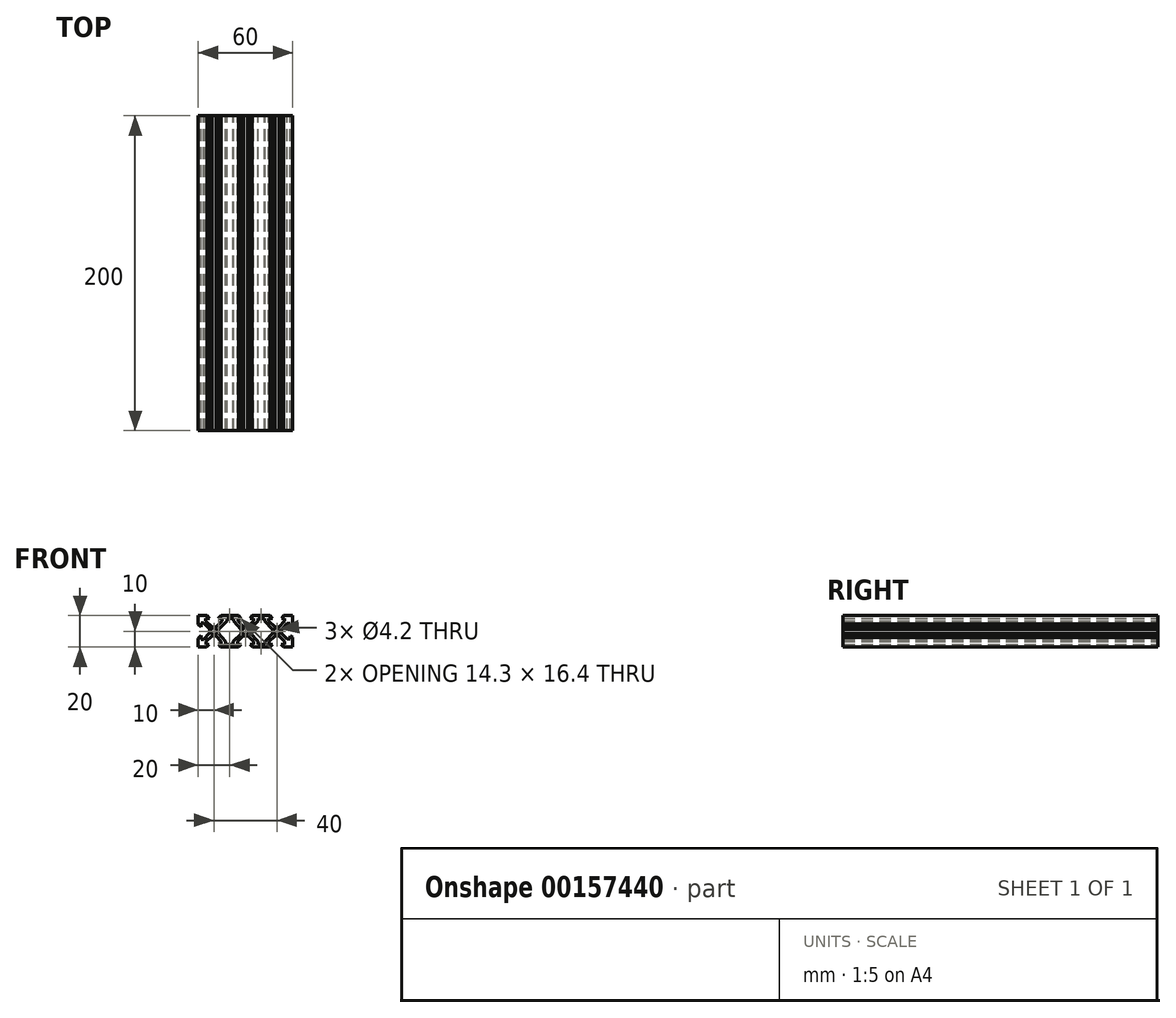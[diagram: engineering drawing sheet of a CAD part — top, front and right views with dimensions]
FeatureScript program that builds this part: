
annotation { "Feature Type Name" : "Feature", "Feature Type Description" : "" }
export const myFeature = defineFeature(function(context is Context, id is Id, definition is map)
    precondition{}
    {
        {
            var Q0;
            Q0=qCreatedBy(makeId("Front.planeOp"),FACE);
            var sketch = newSketch(context, id + "F0", { "sketchPlane" : qUnion([Q0])});
            skLineSegment(sketch, "E0.bottom", {"start": v(30, 10) * mm, "end": v(24.23, 10) * mm});
            skLineSegment(sketch, "E0.top", {"start": v(30, -10) * mm, "end": v(24.23, -10) * mm});
            skLineSegment(sketch, "E0.left", {"start": v(30, 10) * mm, "end": v(30, 4.56) * mm});
            skLineSegment(sketch, "E0.right", {"start": v(-30, 10) * mm, "end": v(-30, 4.4) * mm});
            skPoint(sketch, "E0.middle", {"position": v(0, 0) * mm});
            skLineSegment(sketch, "E1.0", {"start": v(-28.2, 8.2) * mm, "end": v(-28.2, 2.7) * mm});
            skLineSegment(sketch, "E1.1", {"start": v(28.2, 8.2) * mm, "end": v(22.92, 8.2) * mm});
            skLineSegment(sketch, "E1.2", {"start": v(28.2, 8.2) * mm, "end": v(28.2, 2.93) * mm});
            skLineSegment(sketch, "E1.3", {"start": v(28.2, -8.2) * mm, "end": v(22.78, -8.2) * mm});
            skCircle(sketch, "E2", {"center": v(0, 0) * mm, "radius": 2.1 * mm});
            skCircle(sketch, "E3", {"center": v(-20, 0) * mm, "radius": 2.1 * mm});
            skCircle(sketch, "E4", {"center": v(20, 0) * mm, "radius": 2.1 * mm});
            skLineSegment(sketch, "E5", {"start": v(-30, 4.4) * mm, "end": v(-28.2, 2.7) * mm});
            skLineSegment(sketch, "E6", {"start": v(-30, -4.47) * mm, "end": v(-28.2, -2.76) * mm});
            skLineSegment(sketch, "E7", {"start": v(-24.21, 10) * mm, "end": v(-22.7, 8.2) * mm});
            skLineSegment(sketch, "E8", {"start": v(-17.28, 8.2) * mm, "end": v(-15.53, 10) * mm});
            skLineSegment(sketch, "E9", {"start": v(-24.77, -10) * mm, "end": v(-23.06, -8.2) * mm});
            skLineSegment(sketch, "E10", {"start": v(-17.09, -8.2) * mm, "end": v(-15.66, -10) * mm});
            skLineSegment(sketch, "E11", {"start": v(2.9, 8.2) * mm, "end": v(4.22, 10) * mm});
            skLineSegment(sketch, "E12", {"start": v(-4.42, -10) * mm, "end": v(-2.88, -8.2) * mm});
            skLineSegment(sketch, "E13", {"start": v(2.82, -8.2) * mm, "end": v(4.44, -10) * mm});
            skLineSegment(sketch, "E14", {"start": v(15.72, 10) * mm, "end": v(17.27, 8.2) * mm});
            skLineSegment(sketch, "E15", {"start": v(22.92, 8.2) * mm, "end": v(24.23, 10) * mm});
            skLineSegment(sketch, "E16", {"start": v(15.6, -10) * mm, "end": v(17.12, -8.2) * mm});
            skLineSegment(sketch, "E17", {"start": v(22.78, -8.2) * mm, "end": v(24.23, -10) * mm});
            skLineSegment(sketch, "E18", {"start": v(28.2, -2.83) * mm, "end": v(30, -4) * mm});
            skLineSegment(sketch, "E19", {"start": v(28.2, 2.93) * mm, "end": v(30, 4.56) * mm});
            skLineSegment(sketch, "E20.bottom", {"start": v(-17.15, 2.85) * mm, "end": v(-22.85, 2.85) * mm});
            skLineSegment(sketch, "E20.top", {"start": v(-17.15, -2.85) * mm, "end": v(-22.85, -2.85) * mm});
            skLineSegment(sketch, "E20.left", {"start": v(-17.15, 2.85) * mm, "end": v(-17.15, -2.85) * mm});
            skLineSegment(sketch, "E20.right", {"start": v(-22.85, 2.85) * mm, "end": v(-22.85, -2.85) * mm});
            skLineSegment(sketch, "E21.bottom", {"start": v(2.85, 2.85) * mm, "end": v(-2.85, 2.85) * mm});
            skLineSegment(sketch, "E21.top", {"start": v(2.85, -2.85) * mm, "end": v(-2.85, -2.85) * mm});
            skLineSegment(sketch, "E21.left", {"start": v(2.85, 2.85) * mm, "end": v(2.85, -2.85) * mm});
            skLineSegment(sketch, "E21.right", {"start": v(-2.85, 2.85) * mm, "end": v(-2.85, -2.85) * mm});
            skLineSegment(sketch, "E22.bottom", {"start": v(22.85, 2.85) * mm, "end": v(17.15, 2.85) * mm});
            skLineSegment(sketch, "E22.top", {"start": v(22.85, -2.85) * mm, "end": v(17.15, -2.85) * mm});
            skLineSegment(sketch, "E22.left", {"start": v(22.85, 2.85) * mm, "end": v(22.85, -2.85) * mm});
            skLineSegment(sketch, "E22.right", {"start": v(17.15, 2.85) * mm, "end": v(17.15, -2.85) * mm});
            skLineSegment(sketch, "E23", {"start": v(-20, 2.1) * mm, "end": v(-44.26, 2.1) * mm, "construction": true});
            skPoint(sketch, "E23.startSnap0", {"position": v(-20, 2.85) * mm});
            skLineSegment(sketch, "E24", {"start": v(-19.99, -2.1) * mm, "end": v(-43.86, -2.1) * mm, "construction": true});
            skLineSegment(sketch, "E25.0", {"start": v(-26.56, 6.56) * mm, "end": v(-26.56, 5.27) * mm});
            skLineSegment(sketch, "E25.1", {"start": v(26.56, 6.56) * mm, "end": v(24.93, 6.56) * mm});
            skLineSegment(sketch, "E25.2", {"start": v(26.56, 6.56) * mm, "end": v(26.56, 4.88) * mm});
            skLineSegment(sketch, "E25.3", {"start": v(26.56, -6.56) * mm, "end": v(24.9, -6.56) * mm});
            skLineSegment(sketch, "E26", {"start": v(-25.2, 6.56) * mm, "end": v(-25.2, 8.2) * mm});
            skLineSegment(sketch, "E27", {"start": v(-26.56, 5.27) * mm, "end": v(-28.2, 5.27) * mm});
            skLineSegment(sketch, "E28", {"start": v(-25.2, 6.56) * mm, "end": v(-21.3, 2.85) * mm});
            skLineSegment(sketch, "E29", {"start": v(-26.56, 5.27) * mm, "end": v(-22.85, 1.46) * mm});
            skLineSegment(sketch, "E30", {"start": v(-26.56, -5.15) * mm, "end": v(-22.85, -1.11) * mm});
            skLineSegment(sketch, "E31", {"start": v(-24.9, -6.56) * mm, "end": v(-21.17, -2.85) * mm});
            skLineSegment(sketch, "E32", {"start": v(-26.56, -5.15) * mm, "end": v(-28.2, -5.15) * mm});
            skLineSegment(sketch, "E33", {"start": v(-24.9, -6.56) * mm, "end": v(-24.9, -8.2) * mm});
            skLineSegment(sketch, "E34", {"start": v(-14.86, 8.2) * mm, "end": v(-14.86, 6.56) * mm});
            skLineSegment(sketch, "E35", {"start": v(-14.86, 6.56) * mm, "end": v(-18.6, 2.85) * mm});
            skLineSegment(sketch, "E36", {"start": v(-17.15, 1.27) * mm, "end": v(-11.83, 6.56) * mm});
            skLineSegment(sketch, "E37", {"start": v(-2.77, 8.2) * mm, "end": v(-4.42, 10) * mm});
            skLineSegment(sketch, "E38", {"start": v(-18.74, -2.85) * mm, "end": v(-15.4, -6.56) * mm});
            skLineSegment(sketch, "E39", {"start": v(-15.4, -6.56) * mm, "end": v(-15.4, -8.2) * mm});
            skLineSegment(sketch, "E40", {"start": v(-17.15, -1.23) * mm, "end": v(-12.58, -6.56) * mm});
            skLineSegment(sketch, "E41", {"start": v(-1.3, 2.85) * mm, "end": v(-4.84, 6.56) * mm});
            skLineSegment(sketch, "E42", {"start": v(-4.84, 6.56) * mm, "end": v(-4.84, 8.2) * mm});
            skLineSegment(sketch, "E43", {"start": v(-2.85, 1.13) * mm, "end": v(-7.54, 6.56) * mm});
            skLineSegment(sketch, "E44", {"start": v(-2.85, -1.54) * mm, "end": v(-7.8, -6.56) * mm});
            skLineSegment(sketch, "E45", {"start": v(-1.46, -2.85) * mm, "end": v(-5.09, -6.56) * mm});
            skLineSegment(sketch, "E46", {"start": v(-5.09, -6.56) * mm, "end": v(-5.09, -8.2) * mm});
            skLineSegment(sketch, "E47", {"start": v(-12.58, -6.56) * mm, "end": v(-12.58, -8.2) * mm});
            skLineSegment(sketch, "E48", {"start": v(-7.8, -6.56) * mm, "end": v(-7.8, -8.2) * mm});
            skLineSegment(sketch, "E49", {"start": v(-7.54, 6.56) * mm, "end": v(-7.54, 8.2) * mm});
            skLineSegment(sketch, "E50", {"start": v(-11.83, 6.56) * mm, "end": v(-11.83, 8.2) * mm});
            skLineSegment(sketch, "E51", {"start": v(1.34, 2.85) * mm, "end": v(5.05, 6.56) * mm});
            skLineSegment(sketch, "E52", {"start": v(2.85, 1.12) * mm, "end": v(8, 6.56) * mm});
            skLineSegment(sketch, "E53", {"start": v(8, 6.56) * mm, "end": v(8, 8.2) * mm});
            skLineSegment(sketch, "E54", {"start": v(1.52, -2.85) * mm, "end": v(5.25, -6.56) * mm});
            skLineSegment(sketch, "E55", {"start": v(5.25, -6.5) * mm, "end": v(5.25, -8.2) * mm});
            skLineSegment(sketch, "E56", {"start": v(2.85, -1.1) * mm, "end": v(8, -6.56) * mm});
            skLineSegment(sketch, "E57", {"start": v(18.75, 2.85) * mm, "end": v(14.61, 6.56) * mm});
            skLineSegment(sketch, "E58", {"start": v(17.15, 1.18) * mm, "end": v(12.15, 6.56) * mm});
            skLineSegment(sketch, "E59", {"start": v(12.15, 6.51) * mm, "end": v(12.15, 8.2) * mm});
            skLineSegment(sketch, "E60", {"start": v(14.61, 6.56) * mm, "end": v(14.61, 8.2) * mm});
            skLineSegment(sketch, "E61", {"start": v(17.15, -1.45) * mm, "end": v(12.58, -6.56) * mm});
            skLineSegment(sketch, "E62", {"start": v(18.78, -2.85) * mm, "end": v(15.13, -6.56) * mm});
            skLineSegment(sketch, "E63", {"start": v(12.58, -6.56) * mm, "end": v(12.58, -8.2) * mm});
            skLineSegment(sketch, "E64", {"start": v(21.38, 2.85) * mm, "end": v(24.93, 6.56) * mm});
            skLineSegment(sketch, "E65", {"start": v(22.85, 1.03) * mm, "end": v(26.56, 4.88) * mm});
            skLineSegment(sketch, "E66", {"start": v(22.85, -1.37) * mm, "end": v(26.56, -4.98) * mm});
            skLineSegment(sketch, "E67", {"start": v(26.5, -4.98) * mm, "end": v(28.2, -4.98) * mm});
            skLineSegment(sketch, "E68", {"start": v(21.27, -2.85) * mm, "end": v(24.9, -6.56) * mm});
            skLineSegment(sketch, "E69", {"start": v(24.9, -6.5) * mm, "end": v(24.9, -8.2) * mm});
            skLineSegment(sketch, "E70.trimOffspring", {"start": v(-24.21, 10) * mm, "end": v(-30, 10) * mm});
            skLineSegment(sketch, "E71.trimOffspring", {"start": v(-22.7, 8.2) * mm, "end": v(-28.2, 8.2) * mm});
            skLineSegment(sketch, "E72.trimOffspring", {"start": v(-25.2, 6.56) * mm, "end": v(-26.56, 6.56) * mm});
            skLineSegment(sketch, "E73.trimOffspring", {"start": v(-28.2, -2.76) * mm, "end": v(-28.2, -8.2) * mm});
            skLineSegment(sketch, "E74.trimOffspring", {"start": v(-30, -4.47) * mm, "end": v(-30, -10) * mm});
            skLineSegment(sketch, "E75.trimOffspring", {"start": v(-26.56, -5.15) * mm, "end": v(-26.56, -6.56) * mm});
            skLineSegment(sketch, "E76.trimOffspring", {"start": v(-11.83, 6.56) * mm, "end": v(-14.86, 6.56) * mm});
            skLineSegment(sketch, "E77.trimOffspring", {"start": v(-12.58, -6.56) * mm, "end": v(-15.4, -6.56) * mm});
            skLineSegment(sketch, "E78.trimOffspring", {"start": v(-24.9, -6.56) * mm, "end": v(-26.56, -6.56) * mm});
            skLineSegment(sketch, "E79.trimOffspring", {"start": v(-23.06, -8.2) * mm, "end": v(-28.2, -8.2) * mm});
            skLineSegment(sketch, "E80.trimOffspring", {"start": v(-24.77, -10) * mm, "end": v(-30, -10) * mm});
            skLineSegment(sketch, "E81.trimOffspring", {"start": v(-4.42, 10) * mm, "end": v(-15.53, 10) * mm});
            skLineSegment(sketch, "E82", {"start": v(5.05, 6.56) * mm, "end": v(5.05, 8.2) * mm});
            skLineSegment(sketch, "E83.trimOffspring", {"start": v(-2.77, 8.2) * mm, "end": v(-17.28, 8.2) * mm});
            skLineSegment(sketch, "E84.trimOffspring", {"start": v(-4.84, 6.56) * mm, "end": v(-7.54, 6.56) * mm});
            skLineSegment(sketch, "E85.trimOffspring", {"start": v(8, 6.56) * mm, "end": v(5.05, 6.56) * mm});
            skLineSegment(sketch, "E86.trimOffspring", {"start": v(8, -6.56) * mm, "end": v(5.25, -6.56) * mm});
            skLineSegment(sketch, "E87.trimOffspring", {"start": v(-4.42, -10) * mm, "end": v(-15.66, -10) * mm});
            skLineSegment(sketch, "E88.trimOffspring", {"start": v(-2.88, -8.2) * mm, "end": v(-17.09, -8.2) * mm});
            skLineSegment(sketch, "E89.trimOffspring", {"start": v(-5.09, -6.56) * mm, "end": v(-7.8, -6.56) * mm});
            skLineSegment(sketch, "E90.trimOffspring", {"start": v(15.6, -10) * mm, "end": v(4.44, -10) * mm});
            skLineSegment(sketch, "E91", {"start": v(15.13, -6.56) * mm, "end": v(15.13, -8.2) * mm});
            skLineSegment(sketch, "E92.trimOffspring", {"start": v(17.12, -8.2) * mm, "end": v(2.82, -8.2) * mm});
            skLineSegment(sketch, "E93.trimOffspring", {"start": v(15.13, -6.56) * mm, "end": v(12.58, -6.56) * mm});
            skLineSegment(sketch, "E94.trimOffspring", {"start": v(30, -4) * mm, "end": v(30, -10) * mm});
            skLineSegment(sketch, "E95.trimOffspring", {"start": v(28.2, -2.83) * mm, "end": v(28.2, -8.2) * mm});
            skLineSegment(sketch, "E96.trimOffspring", {"start": v(26.56, -4.98) * mm, "end": v(26.56, -6.56) * mm});
            skLineSegment(sketch, "E97", {"start": v(24.93, 6.56) * mm, "end": v(24.93, 8.2) * mm});
            skLineSegment(sketch, "E98", {"start": v(26.56, 4.88) * mm, "end": v(28.2, 4.88) * mm});
            skLineSegment(sketch, "E99.trimOffspring", {"start": v(15.72, 10) * mm, "end": v(4.22, 10) * mm});
            skLineSegment(sketch, "E100.trimOffspring", {"start": v(17.27, 8.2) * mm, "end": v(2.9, 8.2) * mm});
            skLineSegment(sketch, "E101.trimOffspring", {"start": v(14.61, 6.56) * mm, "end": v(12.15, 6.56) * mm});
            skLineSegment(sketch, "E102", {"start": v(8, -6.56) * mm, "end": v(8, -8.2) * mm});
            skSolve(sketch);
        }
        {
            var Q0;
            Q0=makeQuery(id+"F0.imprint","IMPRINT",FACE,{"disambiguationData":[TD([[makeQuery(id+"F0.imprint","IMPRINT",EDGE,{"derivedFrom":sQuery(id+"F0.wireOp",EDGE,"E0.bottom")}),1.0]])]});
            var Q1;
            Q1=makeQuery(id+"F0.imprint","IMPRINT",FACE,{"disambiguationData":[TD([[makeQuery(id+"F0.imprint","IMPRINT",EDGE,{"derivedFrom":sQuery(id+"F0.wireOp",EDGE,"E25.1")}),-1.0]])]});
            var Q2;
            Q2=makeQuery(id+"F0.imprint","IMPRINT",FACE,{"disambiguationData":[TD([[makeQuery(id+"F0.imprint","IMPRINT",EDGE,{"derivedFrom":sQuery(id+"F0.wireOp",EDGE,"E25.1")}),1.0]])]});
            var Q3;
            {var subQ1=sQuery(id+"F0.wireOp",EDGE,"E25.3");Q3=makeQuery(id+"F0.imprint","IMPRINT",FACE,{"disambiguationData":[TD([[makeQuery(id+"F0.imprint","IMPRINT",EDGE,{"derivedFrom":subQ1}),1.0]])]});}
            var Q4;
            Q4=makeQuery(id+"F0.imprint","IMPRINT",FACE,{"disambiguationData":[TD([[makeQuery(id+"F0.imprint","IMPRINT",EDGE,{"derivedFrom":sQuery(id+"F0.wireOp",EDGE,"E0.top")}),-1.0]])]});
            var Q5;
            Q5=makeQuery(id+"F0.imprint","IMPRINT",FACE,{"disambiguationData":[TD([[makeQuery(id+"F0.imprint","IMPRINT",EDGE,{"derivedFrom":sQuery(id+"F0.wireOp",EDGE,"E25.3")}),-1.0]])]});
            var Q6;
            Q6=makeQuery(id+"F0.imprint","IMPRINT",FACE,{"disambiguationData":[TD([[makeQuery(id+"F0.imprint","IMPRINT",EDGE,{"derivedFrom":sQuery(id+"F0.wireOp",EDGE,"E4")}),-1.0]])]});
            var Q7;
            {var subQ1=sQuery(id+"F0.wireOp",EDGE,"E57");Q7=makeQuery(id+"F0.imprint","IMPRINT",FACE,{"disambiguationData":[TD([[makeQuery(id+"F0.imprint","IMPRINT",EDGE,{"derivedFrom":subQ1}),1.0]])]});}
            var Q8;
            {var subQ4=sQuery(id+"F0.wireOp",EDGE,"E60");Q8=makeQuery(id+"F0.imprint","IMPRINT",FACE,{"disambiguationData":[TD([[makeQuery(id+"F0.imprint","IMPRINT",EDGE,{"derivedFrom":subQ4}),1.0]])]});}
            var Q9;
            {var subQ3=sQuery(id+"F0.wireOp",EDGE,"E11");Q9=makeQuery(id+"F0.imprint","IMPRINT",FACE,{"disambiguationData":[TD([[makeQuery(id+"F0.imprint","IMPRINT",EDGE,{"derivedFrom":subQ3}),-1.0]])]});}
            var Q10;
            {var subQ0=sQuery(id+"F0.wireOp",EDGE,"E53");Q10=makeQuery(id+"F0.imprint","IMPRINT",FACE,{"disambiguationData":[TD([[makeQuery(id+"F0.imprint","IMPRINT",EDGE,{"derivedFrom":subQ0}),1.0]])]});}
            var Q11;
            {var subQ1=sQuery(id+"F0.wireOp",EDGE,"E51");Q11=makeQuery(id+"F0.imprint","IMPRINT",FACE,{"disambiguationData":[TD([[makeQuery(id+"F0.imprint","IMPRINT",EDGE,{"derivedFrom":subQ1}),-1.0]])]});}
            var Q12;
            {var subQ4=sQuery(id+"F0.wireOp",EDGE,"E61");Q12=makeQuery(id+"F0.imprint","IMPRINT",FACE,{"disambiguationData":[TD([[makeQuery(id+"F0.imprint","IMPRINT",EDGE,{"derivedFrom":subQ4}),1.0]])]});}
            var Q13;
            {var subQ0=sQuery(id+"F0.wireOp",EDGE,"E63");Q13=makeQuery(id+"F0.imprint","IMPRINT",FACE,{"disambiguationData":[TD([[makeQuery(id+"F0.imprint","IMPRINT",EDGE,{"derivedFrom":subQ0}),1.0]])]});}
            var Q14;
            {var subQ3=sQuery(id+"F0.wireOp",EDGE,"E13");Q14=makeQuery(id+"F0.imprint","IMPRINT",FACE,{"disambiguationData":[TD([[makeQuery(id+"F0.imprint","IMPRINT",EDGE,{"derivedFrom":subQ3}),1.0]])]});}
            var Q15;
            {var subQ0=sQuery(id+"F0.wireOp",EDGE,"E86.trimOffspring");Q15=makeQuery(id+"F0.imprint","IMPRINT",FACE,{"disambiguationData":[TD([[makeQuery(id+"F0.imprint","IMPRINT",EDGE,{"derivedFrom":subQ0}),1.0]])]});}
            var Q16;
            {var subQ1=sQuery(id+"F0.wireOp",EDGE,"E54");Q16=makeQuery(id+"F0.imprint","IMPRINT",FACE,{"disambiguationData":[TD([[makeQuery(id+"F0.imprint","IMPRINT",EDGE,{"derivedFrom":subQ1}),1.0]])]});}
            var Q17;
            Q17=makeQuery(id+"F0.imprint","IMPRINT",FACE,{"disambiguationData":[TD([[makeQuery(id+"F0.imprint","IMPRINT",EDGE,{"derivedFrom":sQuery(id+"F0.wireOp",EDGE,"E2")}),-1.0]])]});
            var Q18;
            {var subQ0=sQuery(id+"F0.wireOp",EDGE,"E41");Q18=makeQuery(id+"F0.imprint","IMPRINT",FACE,{"disambiguationData":[TD([[makeQuery(id+"F0.imprint","IMPRINT",EDGE,{"derivedFrom":subQ0}),1.0]])]});}
            var Q19;
            {var subQ0=sQuery(id+"F0.wireOp",EDGE,"E42");Q19=makeQuery(id+"F0.imprint","IMPRINT",FACE,{"disambiguationData":[TD([[makeQuery(id+"F0.imprint","IMPRINT",EDGE,{"derivedFrom":subQ0}),1.0]])]});}
            var Q20;
            {var subQ5=sQuery(id+"F0.wireOp",EDGE,"E8");Q20=makeQuery(id+"F0.imprint","IMPRINT",FACE,{"disambiguationData":[TD([[makeQuery(id+"F0.imprint","IMPRINT",EDGE,{"derivedFrom":subQ5}),-1.0]])]});}
            var Q21;
            {var subQ0=sQuery(id+"F0.wireOp",EDGE,"E34");Q21=makeQuery(id+"F0.imprint","IMPRINT",FACE,{"disambiguationData":[TD([[makeQuery(id+"F0.imprint","IMPRINT",EDGE,{"derivedFrom":subQ0}),1.0]])]});}
            var Q22;
            {var subQ0=sQuery(id+"F0.wireOp",EDGE,"E35");Q22=makeQuery(id+"F0.imprint","IMPRINT",FACE,{"disambiguationData":[TD([[makeQuery(id+"F0.imprint","IMPRINT",EDGE,{"derivedFrom":subQ0}),1.0]])]});}
            var Q23;
            {var subQ1=sQuery(id+"F0.wireOp",EDGE,"E44");Q23=makeQuery(id+"F0.imprint","IMPRINT",FACE,{"disambiguationData":[TD([[makeQuery(id+"F0.imprint","IMPRINT",EDGE,{"derivedFrom":subQ1}),1.0]])]});}
            var Q24;
            {var subQ0=sQuery(id+"F0.wireOp",EDGE,"E46");Q24=makeQuery(id+"F0.imprint","IMPRINT",FACE,{"disambiguationData":[TD([[makeQuery(id+"F0.imprint","IMPRINT",EDGE,{"derivedFrom":subQ0}),-1.0]])]});}
            var Q25;
            {var subQ3=sQuery(id+"F0.wireOp",EDGE,"E10");Q25=makeQuery(id+"F0.imprint","IMPRINT",FACE,{"disambiguationData":[TD([[makeQuery(id+"F0.imprint","IMPRINT",EDGE,{"derivedFrom":subQ3}),1.0]])]});}
            var Q26;
            {var subQ0=sQuery(id+"F0.wireOp",EDGE,"E39");Q26=makeQuery(id+"F0.imprint","IMPRINT",FACE,{"disambiguationData":[TD([[makeQuery(id+"F0.imprint","IMPRINT",EDGE,{"derivedFrom":subQ0}),1.0]])]});}
            var Q27;
            {var subQ0=sQuery(id+"F0.wireOp",EDGE,"E38");Q27=makeQuery(id+"F0.imprint","IMPRINT",FACE,{"disambiguationData":[TD([[makeQuery(id+"F0.imprint","IMPRINT",EDGE,{"derivedFrom":subQ0}),1.0]])]});}
            var Q28;
            Q28=makeQuery(id+"F0.imprint","IMPRINT",FACE,{"disambiguationData":[TD([[makeQuery(id+"F0.imprint","IMPRINT",EDGE,{"derivedFrom":sQuery(id+"F0.wireOp",EDGE,"E3")}),-1.0]])]});
            var Q29;
            Q29=makeQuery(id+"F0.imprint","IMPRINT",FACE,{"disambiguationData":[TD([[makeQuery(id+"F0.imprint","IMPRINT",EDGE,{"derivedFrom":sQuery(id+"F0.wireOp",EDGE,"E25.0")}),1.0]])]});
            var Q30;
            {var subQ1=sQuery(id+"F0.wireOp",EDGE,"E30");Q30=makeQuery(id+"F0.imprint","IMPRINT",FACE,{"disambiguationData":[TD([[makeQuery(id+"F0.imprint","IMPRINT",EDGE,{"derivedFrom":subQ1}),-1.0]])]});}
            var Q31;
            Q31=makeQuery(id+"F0.imprint","IMPRINT",FACE,{"disambiguationData":[TD([[makeQuery(id+"F0.imprint","IMPRINT",EDGE,{"derivedFrom":sQuery(id+"F0.wireOp",EDGE,"E25.0")}),-1.0]])]});
            var Q32;
            Q32=makeQuery(id+"F0.imprint","IMPRINT",FACE,{"disambiguationData":[TD([[makeQuery(id+"F0.imprint","IMPRINT",EDGE,{"derivedFrom":sQuery(id+"F0.wireOp",EDGE,"E0.right")}),1.0]])]});
            var Q33;
            {var subQ1=sQuery(id+"F0.wireOp",EDGE,"E32");Q33=makeQuery(id+"F0.imprint","IMPRINT",FACE,{"disambiguationData":[TD([[makeQuery(id+"F0.imprint","IMPRINT",EDGE,{"derivedFrom":subQ1}),1.0]])]});}
            var Q34;
            {var subQ4=sQuery(id+"F0.wireOp",EDGE,"E6");Q34=makeQuery(id+"F0.imprint","IMPRINT",FACE,{"disambiguationData":[TD([[makeQuery(id+"F0.imprint","IMPRINT",EDGE,{"derivedFrom":subQ4}),-1.0]])]});}
            extrude(context, id + "F1", {"entities" : qUnion([Q0, Q1, Q2, Q3, Q4, Q5, Q6, Q7, Q8, Q9, Q10, Q11, Q12, Q13, Q14, Q15, Q16, Q17, Q18, Q19, Q20, Q21, Q22, Q23, Q24, Q25, Q26, Q27, Q28, Q29, Q30, Q31, Q32, Q33, Q34]), "depth" : 200 * mm});
        }
    });
